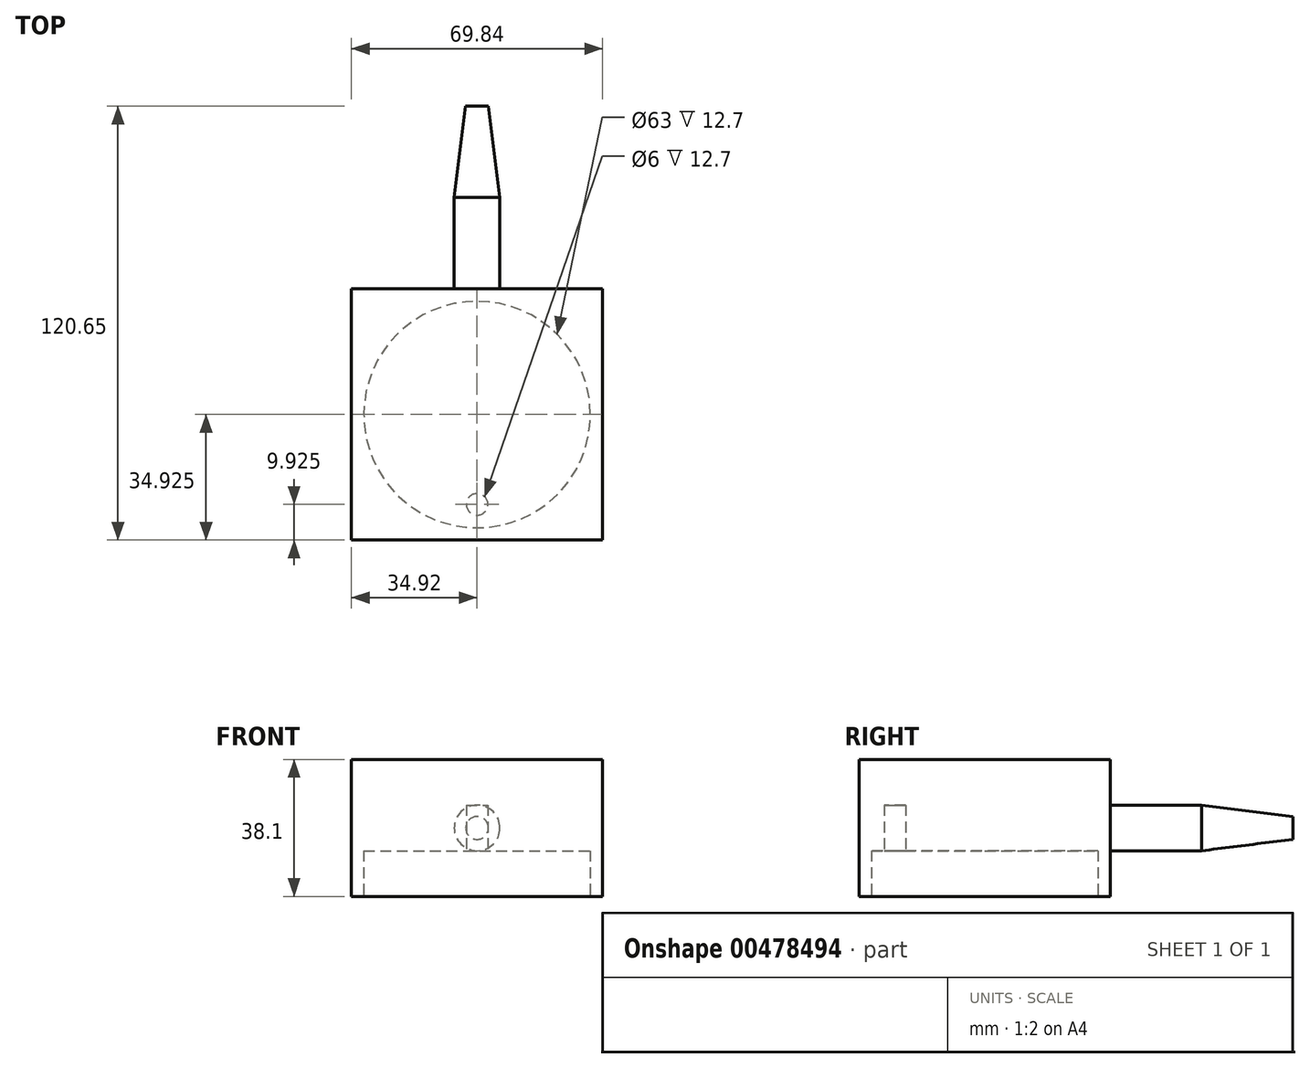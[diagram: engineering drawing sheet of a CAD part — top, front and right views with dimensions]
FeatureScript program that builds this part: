
annotation { "Feature Type Name" : "Feature", "Feature Type Description" : "" }
export const myFeature = defineFeature(function(context is Context, id is Id, definition is map)
    precondition{}
    {
        {
            var Q0;
            Q0=qCreatedBy(makeId("Right.planeOp"),FACE);
            var sketch = newSketch(context, id + "F0", { "sketchPlane" : qUnion([Q0])});
            skLineSegment(sketch, "E0", {"start": v(0, 0) * mm, "end": v(50.8, 0) * mm});
            skLineSegment(sketch, "E1", {"start": v(50.8, 0) * mm, "end": v(50.8, 3.18) * mm});
            skLineSegment(sketch, "E2", {"start": v(50.8, 3.18) * mm, "end": v(25.4, 6.35) * mm});
            skLineSegment(sketch, "E3", {"start": v(25.4, 6.35) * mm, "end": v(0, 6.35) * mm});
            skLineSegment(sketch, "E4", {"start": v(0, 6.35) * mm, "end": v(0, 0) * mm});
            skSolve(sketch);
        }
        {
            var Q0;
            Q0 = qSketchRegion(id + "F0", true);
            var Q1;
            Q1=sQuery(id+"F0.wireOp",EDGE,"E0");
            revolve(context, id + "F1", {"entities" : qUnion([Q0]), "axis" : qUnion([Q1]), "revolveType" : RevolveType.FULL});
        }
        {
            var Q0;
            Q0=qCreatedBy(makeId("Front.planeOp"),FACE);
            var sketch = newSketch(context, id + "F2", { "sketchPlane" : qUnion([Q0])});
            skLineSegment(sketch, "E5.bottom", {"start": v(34.93, 19.05) * mm, "end": v(-34.92, 19.05) * mm});
            skLineSegment(sketch, "E5.top", {"start": v(34.92, -19.05) * mm, "end": v(-34.93, -19.05) * mm});
            skLineSegment(sketch, "E5.left", {"start": v(34.93, 19.05) * mm, "end": v(34.92, -19.05) * mm});
            skLineSegment(sketch, "E5.right", {"start": v(-34.92, 19.05) * mm, "end": v(-34.93, -19.05) * mm});
            skPoint(sketch, "E5.middle", {"position": v(0, 0) * mm});
            skSolve(sketch);
        }
        {
            var Q0;
            Q0 = qSketchRegion(id + "F2", true);
            extrude(context, id + "F3", {"entities" : qUnion([Q0]), "operationType" : NewBodyOperationType.ADD, "depth" : 69.85 * mm});
        }
        {
            var Q0;
            Q0=makeQuery(id+"F3.opExtrude","SWEPT_FACE",FACE,{"disambiguationData":[OSD([sQuery(id+"F2.wireOp",EDGE,"E5.top")])]});
            var sketch = newSketch(context, id + "F4", { "sketchPlane" : qUnion([Q0])});
            skLineSegment(sketch, "E6", {"start": v(0, 69.85) * mm, "end": v(0, 0) * mm, "construction": true});
            skCircle(sketch, "E7", {"center": v(0, 34.93) * mm, "radius": 31.5 * mm});
            skCircle(sketch, "E8", {"center": v(0, 34.93) * mm, "radius": 25 * mm, "construction": true});
            skCircle(sketch, "E9", {"center": v(0, 59.93) * mm, "radius": 3 * mm});
            skSolve(sketch);
        }
        {
            var Q0;
            Q0=makeQuery(id+"F4.imprint","IMPRINT",FACE,{"disambiguationData":[TD([[makeQuery(id+"F4.imprint","IMPRINT",EDGE,{"derivedFrom":sQuery(id+"F4.wireOp",EDGE,"E9")}),1.0]])]});
            var Q1;
            Q1=makeQuery(id+"F4.imprint","IMPRINT",FACE,{"disambiguationData":[TD([[makeQuery(id+"F4.imprint","IMPRINT",EDGE,{"derivedFrom":sQuery(id+"F4.wireOp",EDGE,"E7")}),1.0]])]});
            extrude(context, id + "F5", {"entities" : qUnion([Q0, Q1]), "operationType" : NewBodyOperationType.REMOVE, "oppositeDirection" : true, "depth" : 12.7 * mm});
        }
        {
            var Q0;
            Q0=makeQuery(id+"F4.imprint","IMPRINT",FACE,{"disambiguationData":[TD([[makeQuery(id+"F4.imprint","IMPRINT",EDGE,{"derivedFrom":sQuery(id+"F4.wireOp",EDGE,"E9")}),1.0]])]});
            extrude(context, id + "F6", {"entities" : qUnion([Q0]), "operationType" : NewBodyOperationType.REMOVE, "oppositeDirection" : true, "depth" : 25.4 * mm});
        }
    });
